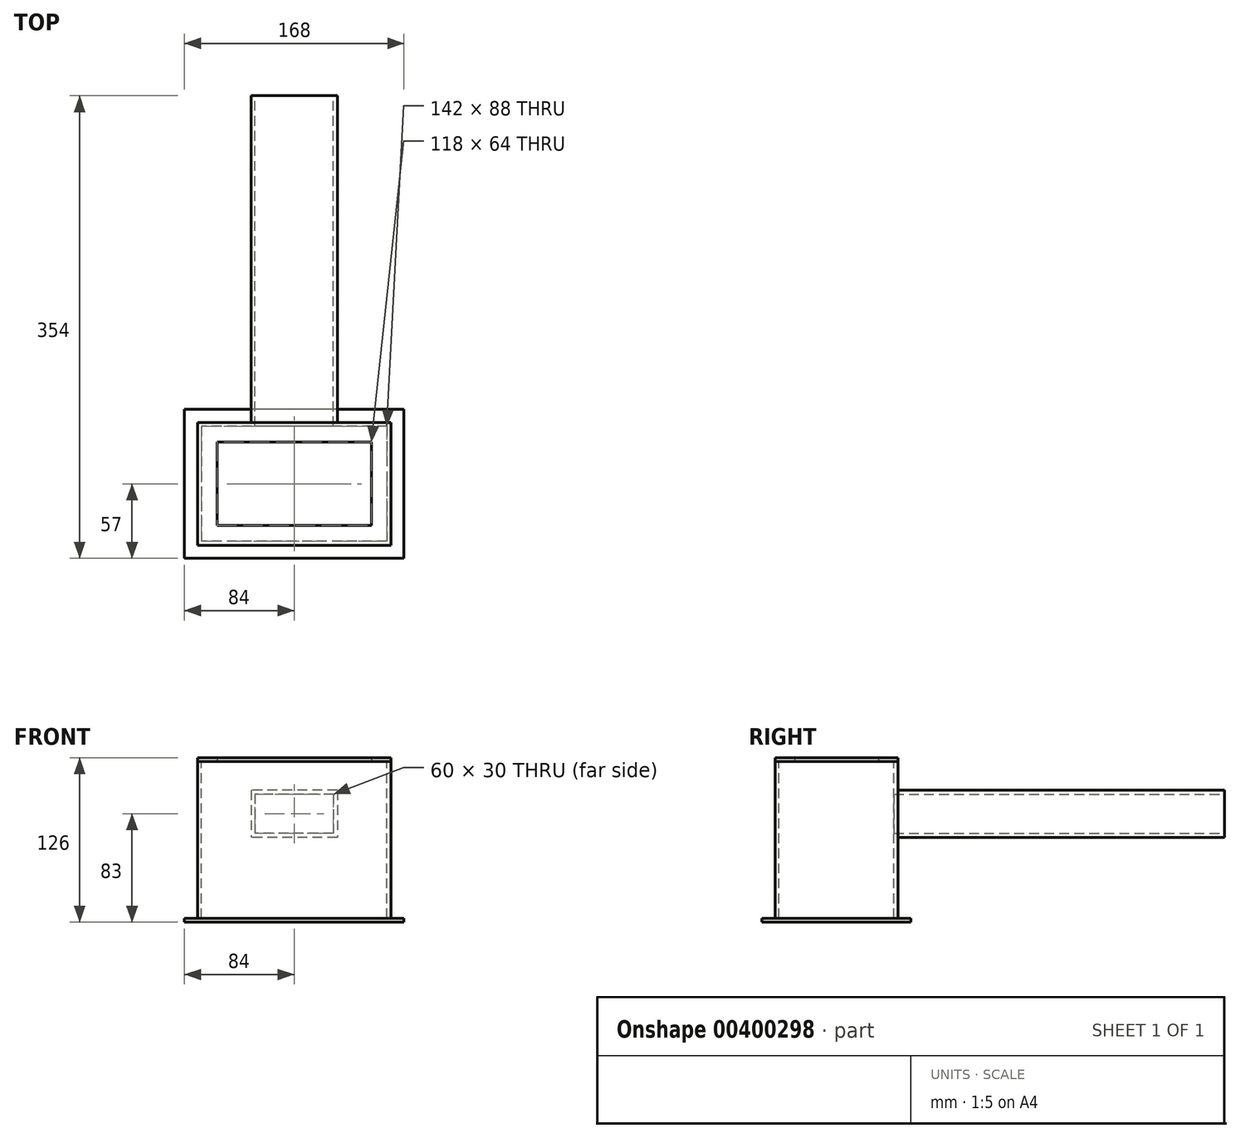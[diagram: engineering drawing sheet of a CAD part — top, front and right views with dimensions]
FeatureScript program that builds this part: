
annotation { "Feature Type Name" : "Feature", "Feature Type Description" : "" }
export const myFeature = defineFeature(function(context is Context, id is Id, definition is map)
    precondition{}
    {
        {
            var Q0;
            Q0=qCreatedBy(makeId("Top.planeOp"),FACE);
            var sketch = newSketch(context, id + "F0", { "sketchPlane" : qUnion([Q0])});
            skLineSegment(sketch, "E0.bottom", {"start": v(59, 32) * mm, "end": v(-59, 32) * mm});
            skLineSegment(sketch, "E0.top", {"start": v(59, -32) * mm, "end": v(-59, -32) * mm});
            skLineSegment(sketch, "E0.left", {"start": v(59, 32) * mm, "end": v(59, -32) * mm});
            skLineSegment(sketch, "E0.right", {"start": v(-59, 32) * mm, "end": v(-59, -32) * mm});
            skPoint(sketch, "E0.middle", {"position": v(0, 0) * mm});
            skLineSegment(sketch, "E1.bottom", {"start": v(74, 47) * mm, "end": v(-74, 47) * mm});
            skLineSegment(sketch, "E1.top", {"start": v(74, -47) * mm, "end": v(-74, -47) * mm});
            skLineSegment(sketch, "E1.left", {"start": v(74, 47) * mm, "end": v(74, -47) * mm});
            skLineSegment(sketch, "E1.right", {"start": v(-74, 47) * mm, "end": v(-74, -47) * mm});
            skSolve(sketch);
        }
        {
            var Q0;
            Q0=makeQuery(id+"F0.imprint","IMPRINT",FACE,{"disambiguationData":[TD([[makeQuery(id+"F0.imprint","IMPRINT",EDGE,{"derivedFrom":sQuery(id+"F0.wireOp",EDGE,"E0.bottom")}),-1.0]])]});
            extrude(context, id + "F1", {"entities" : qUnion([Q0]), "depth" : 3 * mm});
        }
        {
            var Q0;
            Q0=makeQuery(id+"F1.opExtrude","CAP_FACE",FACE,{"disambiguationData":[OSD([sQuery(id+"F0.wireOp",EDGE,"E0.bottom"),sQuery(id+"F0.wireOp",EDGE,"E0.top"),sQuery(id+"F0.wireOp",EDGE,"E0.left"),sQuery(id+"F0.wireOp",EDGE,"E0.right"),sQuery(id+"F0.wireOp",EDGE,"E1.bottom"),sQuery(id+"F0.wireOp",EDGE,"E1.top"),sQuery(id+"F0.wireOp",EDGE,"E1.left"),sQuery(id+"F0.wireOp",EDGE,"E1.right")])],"isStart":true});
            var sketch = newSketch(context, id + "F2", { "sketchPlane" : qUnion([Q0])});
            skLineSegment(sketch, "E2.0", {"start": v(71, 44) * mm, "end": v(-71, 44) * mm});
            skLineSegment(sketch, "E2.1", {"start": v(71, -44) * mm, "end": v(71, 44) * mm});
            skLineSegment(sketch, "E2.2", {"start": v(71, -44) * mm, "end": v(-71, -44) * mm});
            skLineSegment(sketch, "E2.3", {"start": v(-71, -44) * mm, "end": v(-71, 44) * mm});
            skSolve(sketch);
        }
        {
            var Q0;
            Q0=makeQuery(id+"F2.imprint","IMPRINT",FACE,{"disambiguationData":[TD([[makeQuery(id+"F2.imprint","IMPRINT",EDGE,{"derivedFrom":sQuery(id+"F2.wireOp",EDGE,"E2.0")}),-1.0]])]});
            extrude(context, id + "F3", {"entities" : qUnion([Q0]), "depth" : 120 * mm});
        }
        {
            var Q0;
            Q0=makeQuery(id+"F3.opExtrude","SWEPT_FACE",FACE,{"disambiguationData":[OSD([sQuery(id+"F0.wireOp",EDGE,"E1.bottom")])]});
            var sketch = newSketch(context, id + "F4", { "sketchPlane" : qUnion([Q0])});
            skLineSegment(sketch, "E3.bottom", {"start": v(-30, -25) * mm, "end": v(30, -25) * mm});
            skLineSegment(sketch, "E3.top", {"start": v(-30, -55) * mm, "end": v(30, -55) * mm});
            skLineSegment(sketch, "E3.left", {"start": v(-30, -25) * mm, "end": v(-30, -55) * mm});
            skLineSegment(sketch, "E3.right", {"start": v(30, -25) * mm, "end": v(30, -55) * mm});
            skLineSegment(sketch, "E4", {"start": v(0, 0) * mm, "end": v(0, -80.03) * mm, "construction": true});
            skSolve(sketch);
        }
        {
            var Q0;
            Q0=makeQuery(id+"F4.imprint","IMPRINT",FACE,{"disambiguationData":[TD([[makeQuery(id+"F4.imprint","IMPRINT",EDGE,{"derivedFrom":sQuery(id+"F4.wireOp",EDGE,"E3.bottom")}),-1.0]])]});
            extrude(context, id + "F5", {"entities" : qUnion([Q0]), "operationType" : NewBodyOperationType.REMOVE, "oppositeDirection" : true, "depth" : 4 * mm});
        }
        {
            var Q0;
            Q0=makeQuery(id+"F3.opExtrude","CAP_FACE",FACE,{"disambiguationData":[OSD([sQuery(id+"F0.wireOp",EDGE,"E1.bottom"),sQuery(id+"F0.wireOp",EDGE,"E1.top"),sQuery(id+"F0.wireOp",EDGE,"E1.left"),sQuery(id+"F0.wireOp",EDGE,"E1.right"),sQuery(id+"F2.wireOp",EDGE,"E2.0"),sQuery(id+"F2.wireOp",EDGE,"E2.1"),sQuery(id+"F2.wireOp",EDGE,"E2.2"),sQuery(id+"F2.wireOp",EDGE,"E2.3")])],"isStart":false});
            var sketch = newSketch(context, id + "F6", { "sketchPlane" : qUnion([Q0])});
            skLineSegment(sketch, "E5.0", {"start": v(84, 57) * mm, "end": v(-84, 57) * mm});
            skLineSegment(sketch, "E5.1", {"start": v(84, -57) * mm, "end": v(84, 57) * mm});
            skLineSegment(sketch, "E5.2", {"start": v(84, -57) * mm, "end": v(-84, -57) * mm});
            skLineSegment(sketch, "E5.3", {"start": v(-84, -57) * mm, "end": v(-84, 57) * mm});
            skSolve(sketch);
        }
        {
            var Q0;
            Q0=makeQuery(id+"F6.imprint","IMPRINT",FACE,{"disambiguationData":[TD([[makeQuery(id+"F6.imprint","IMPRINT",EDGE,{"derivedFrom":sQuery(id+"F6.wireOp",EDGE,"E5.0")}),1.0]])]});
            var Q1;
            Q1=makeQuery(id+"F6.imprint","IMPRINT",FACE,{"disambiguationData":[TD([[makeQuery(id+"F6.imprint","IMPRINT",EDGE,{"derivedFrom":makeQuery(id+"F3.opExtrude","CAP_EDGE",EDGE,{"disambiguationData":[OSD([sQuery(id+"F2.wireOp",EDGE,"E2.0")])],"isStart":false})}),-1.0]])]});
            var Q2;
            Q2=makeQuery(id+"F6.imprint","IMPRINT",FACE,{"disambiguationData":[TD([[makeQuery(id+"F6.imprint","IMPRINT",EDGE,{"derivedFrom":makeQuery(id+"F3.opExtrude","CAP_EDGE",EDGE,{"disambiguationData":[OSD([sQuery(id+"F2.wireOp",EDGE,"E2.0")])],"isStart":false})}),1.0]])]});
            extrude(context, id + "F7", {"entities" : qUnion([Q0, Q1, Q2]), "depth" : 3 * mm});
        }
        {
            var Q0;
            Q0=makeQuery(id+"F3.opExtrude","SWEPT_FACE",FACE,{"disambiguationData":[OSD([sQuery(id+"F0.wireOp",EDGE,"E1.bottom")])]});
            var sketch = newSketch(context, id + "F8", { "sketchPlane" : qUnion([Q0])});
            skLineSegment(sketch, "E6.0", {"start": v(-33, -22) * mm, "end": v(33, -22) * mm});
            skLineSegment(sketch, "E6.1", {"start": v(-33, -22) * mm, "end": v(-33, -58) * mm});
            skLineSegment(sketch, "E6.2", {"start": v(-33, -58) * mm, "end": v(33, -58) * mm});
            skLineSegment(sketch, "E6.3", {"start": v(33, -22) * mm, "end": v(33, -58) * mm});
            skSolve(sketch);
        }
        {
            var Q0;
            Q0=makeQuery(id+"F8.imprint","IMPRINT",FACE,{"disambiguationData":[TD([[makeQuery(id+"F8.imprint","IMPRINT",EDGE,{"derivedFrom":sQuery(id+"F8.wireOp",EDGE,"E6.0")}),-1.0]])]});
            extrude(context, id + "F9", {"entities" : qUnion([Q0]), "operationType" : NewBodyOperationType.ADD, "depth" : 250 * mm});
        }
    });
